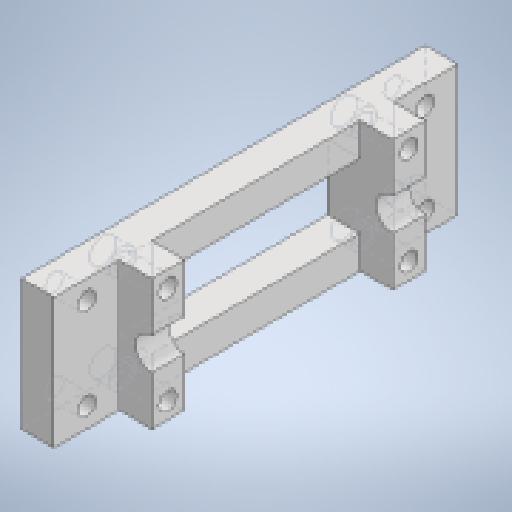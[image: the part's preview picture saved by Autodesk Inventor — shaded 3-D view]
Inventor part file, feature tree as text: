
AUTODESK INVENTOR PART (.ipt)
format: ipt  version: 2023 (Build 270158000, 158)  size: 241,152 bytes
history: native  units: mm
features: extrude x6, sketch x6
ambient origin geometry x8: Origin, YZ Plane, XZ Plane, XY Plane, X Axis, Y Axis, Z Axis, Center Point
bodies: Solid1 (feature_tree)
feature tree (12):
  extrude  "Extrusion1"  Depth=5.0mm
  extrude  "Extrusion2"  Depth=15.0mm
  extrude  "Extrusion3"  Depth=35.0mm
  extrude  "Extrusion4"  Depth=10.0mm
  extrude  "Extrusion5"  Depth=10.0mm
  extrude  "Extrusion6"  Depth=3.0mm TaperAngle=0.0deg
  sketch  "Sketch1"  dims[d0=5.0mm d1=5.0mm]
  sketch  "Sketch2"  dims[d2=5.0mm d3=15.0mm]
  sketch  "Sketch3"  dims[d4=15.0mm d5=35.0mm]
  sketch  "Sketch4"  dims[d6=20.0mm d7=0.0mm d8=10.0mm]
  sketch  "Sketch5"  dims[d9=10.0mm d10=10.0mm]
  sketch  "Sketch6"  dims[d11=5.0mm d12=200.0mm d13=0.0mm d14=5.0mm d15=5.0mm d16=20.0mm d17=0.0mm d18=10.0mm d19=10.0mm d20=3.0mm d21=3.0mm d22=5.0mm d23=5.0mm d24=5.0mm d25=5.0mm d26=3.0mm d27=3.0mm d28=2.75mm d29=2.75mm d30=2.75mm d31=2.75mm d32=5.0mm d33=0.0mm d34=2.5mm d35=2.5mm d36=2.5mm d37=2.5mm d38=2.5mm d39=2.5mm d40=2.5mm d41=2.5mm d42=2.75mm d43=2.75mm d44=2.75mm d45=2.75mm d46=15.0mm d47=0.0mm d48=4.0mm d49=4.0mm d50=4.0mm d51=4.0mm d52=3.0mm d53=0.0mm]
